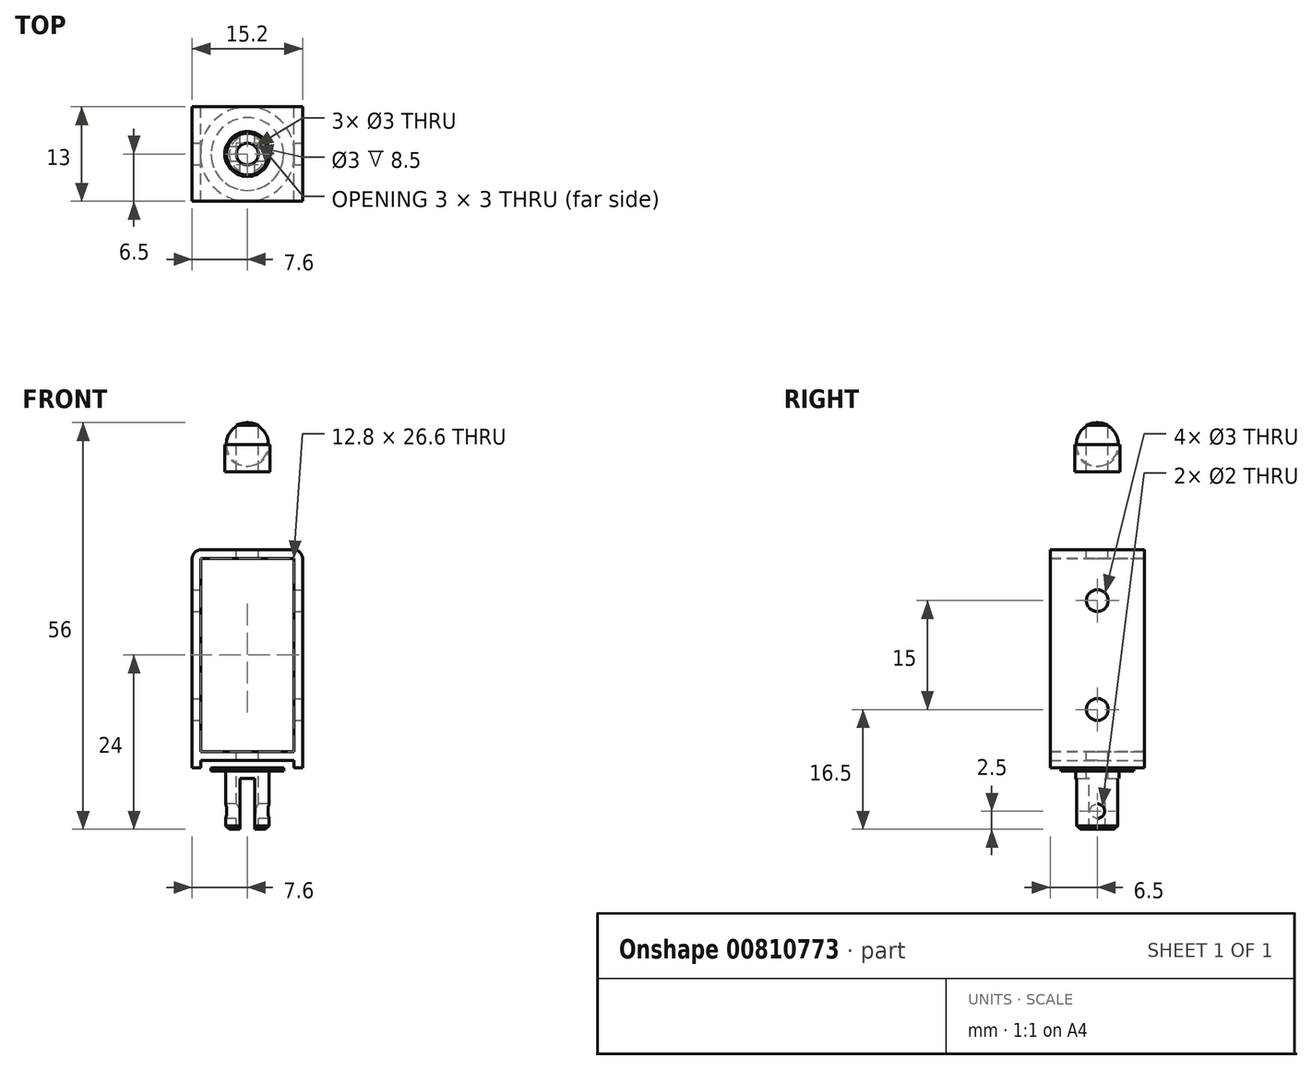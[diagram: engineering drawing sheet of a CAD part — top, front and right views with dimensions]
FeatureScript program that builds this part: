
annotation { "Feature Type Name" : "Feature", "Feature Type Description" : "" }
export const myFeature = defineFeature(function(context is Context, id is Id, definition is map)
    precondition{}
    {
        {
            var Q0;
            Q0=qCreatedBy(makeId("Front.planeOp"),FACE);
            var sketch = newSketch(context, id + "F0", { "sketchPlane" : qUnion([Q0])});
            skLineSegment(sketch, "E0.bottom", {"start": v(7.6, 15) * mm, "end": v(-7.6, 15) * mm});
            skLineSegment(sketch, "E0.top", {"start": v(7.6, -15) * mm, "end": v(-7.6, -15) * mm});
            skLineSegment(sketch, "E0.left", {"start": v(7.6, 15) * mm, "end": v(7.6, -15) * mm});
            skLineSegment(sketch, "E0.right", {"start": v(-7.6, 15) * mm, "end": v(-7.6, -15) * mm});
            skPoint(sketch, "E0.middle", {"position": v(0, 0) * mm});
            skSolve(sketch);
        }
        {
            var Q0;
            Q0=qSketchRegion(id+"F0",true);
            extrude(context, id + "F1", {"entities" : qUnion([Q0]), "depth" : 13 * mm, "symmetric" : true});
        }
        {
            var Q0;
            Q0=qCreatedBy(makeId("Right.planeOp"),FACE);
            var sketch = newSketch(context, id + "F2", { "sketchPlane" : qUnion([Q0])});
            skLineSegment(sketch, "E1", {"start": v(0, 32.5) * mm, "end": v(0, -23.5) * mm});
            skLineSegment(sketch, "E2", {"start": v(0, -23.5) * mm, "end": v(-3, -23.5) * mm});
            skLineSegment(sketch, "E3", {"start": v(-3, -23.5) * mm, "end": v(-3, -15.5) * mm});
            skLineSegment(sketch, "E4", {"start": v(-3, -15.5) * mm, "end": v(-5, -15.5) * mm});
            skLineSegment(sketch, "E5", {"start": v(-5, -15.5) * mm, "end": v(-5, -14.8) * mm});
            skLineSegment(sketch, "E6", {"start": v(-5, -14.8) * mm, "end": v(-1.5, -14.8) * mm});
            skLineSegment(sketch, "E7", {"start": v(-1.5, -14.8) * mm, "end": v(-1.5, 25.75) * mm});
            skLineSegment(sketch, "E8", {"start": v(-1.5, 25.75) * mm, "end": v(-3.1, 25.75) * mm});
            skLineSegment(sketch, "E9", {"start": v(-3.1, 25.75) * mm, "end": v(-3.1, 32.5) * mm});
            skLineSegment(sketch, "E10", {"start": v(-3.1, 32.5) * mm, "end": v(0, 32.5) * mm});
            skSolve(sketch);
        }
        {
            var Q0;
            Q0=qSketchRegion(id+"F2",true);
            var Q1;
            Q1=sQuery(id+"F2.wireOp",EDGE,"E1");
            revolve(context, id + "F3", {"entities" : qUnion([Q0]), "axis" : qUnion([Q1]), "revolveType" : RevolveType.FULL});
        }
        {
            var Q0;
            Q0=makeQuery(id+"F3.opRevolve","SWEPT_EDGE",EDGE,{"disambiguationData":[OSD([sQuery(id+"F2.wireOp",EDGE,"E9"),sQuery(id+"F2.wireOp",EDGE,"E10")])]});
            fillet(context, id + "F4", {"entities" : qUnion([Q0]), "radius" : 3 * mm, "tangentPropagation" : true, "allowEdgeOverflow" : false});
        }
        {
            var Q0;
            Q0=qCreatedBy(makeId("Right.planeOp"),FACE);
            var sketch = newSketch(context, id + "F5", { "sketchPlane" : qUnion([Q0])});
            skLineSegment(sketch, "E11", {"start": v(0, 8) * mm, "end": v(0, -7) * mm, "construction": true});
            skCircle(sketch, "E12", {"center": v(0, 8) * mm, "radius": 1.5 * mm});
            skCircle(sketch, "E13", {"center": v(0, -7) * mm, "radius": 1.5 * mm});
            skLineSegment(sketch, "E14", {"start": v(0, -7) * mm, "end": v(0, -21) * mm, "construction": true});
            skCircle(sketch, "E15", {"center": v(0, -21) * mm, "radius": 1 * mm});
            skSolve(sketch);
        }
        {
            var Q0;
            Q0=makeQuery(id+"F5.imprint","IMPRINT",FACE,{"disambiguationData":[TD([[makeQuery(id+"F5.imprint","IMPRINT",EDGE,{"derivedFrom":sQuery(id+"F5.wireOp",EDGE,"E13")}),1.0]])]});
            var Q1;
            Q1=makeQuery(id+"F5.imprint","IMPRINT",FACE,{"disambiguationData":[TD([[makeQuery(id+"F5.imprint","IMPRINT",EDGE,{"derivedFrom":sQuery(id+"F5.wireOp",EDGE,"E12")}),1.0]])]});
            extrude(context, id + "F6", {"entities" : qUnion([Q0, Q1]), "operationType" : NewBodyOperationType.REMOVE, "endBound" : BoundingType.THROUGH_ALL, "oppositeDirection" : true, "depth" : 25 * mm, "hasSecondDirection" : true, "secondDirectionBound" : BoundingType.THROUGH_ALL, "secondDirectionOppositeDirection" : false, "secondDirectionDepth" : 25 * mm});
        }
        {
            var Q0;
            Q0=makeQuery(id+"F5.imprint","IMPRINT",FACE,{"disambiguationData":[TD([[makeQuery(id+"F5.imprint","IMPRINT",EDGE,{"derivedFrom":sQuery(id+"F5.wireOp",EDGE,"E15")}),1.0]])]});
            extrude(context, id + "F7", {"entities" : qUnion([Q0]), "operationType" : NewBodyOperationType.REMOVE, "endBound" : BoundingType.THROUGH_ALL, "depth" : 25 * mm, "hasSecondDirection" : true, "secondDirectionBound" : BoundingType.THROUGH_ALL, "secondDirectionOppositeDirection" : true, "secondDirectionDepth" : 25 * mm});
        }
        {
            var Q0;
            Q0=qCreatedBy(makeId("Front.planeOp"),FACE);
            var sketch = newSketch(context, id + "F8", { "sketchPlane" : qUnion([Q0])});
            skLineSegment(sketch, "E16.bottom", {"start": v(1, -23.5) * mm, "end": v(-1, -23.5) * mm});
            skLineSegment(sketch, "E16.top", {"start": v(1, -16.5) * mm, "end": v(-1, -16.5) * mm});
            skLineSegment(sketch, "E16.left", {"start": v(1, -23.5) * mm, "end": v(1, -16.5) * mm});
            skLineSegment(sketch, "E16.right", {"start": v(-1, -23.5) * mm, "end": v(-1, -16.5) * mm});
            skPoint(sketch, "E16.middle", {"position": v(0, -20) * mm});
            skSolve(sketch);
        }
        {
            var Q0;
            Q0=makeQuery(id+"F3.opRevolve","SWEPT_EDGE",EDGE,{"disambiguationData":[OSD([sQuery(id+"F2.wireOp",EDGE,"E2"),sQuery(id+"F2.wireOp",EDGE,"E3")])]});
            chamfer(context, id + "F9", {"entities" : qUnion([Q0]), "width" : .5 * mm, "tangentPropagation" : true});
        }
        {
            var Q0;
            Q0=qSketchRegion(id+"F8",true);
            extrude(context, id + "F10", {"entities" : qUnion([Q0]), "operationType" : NewBodyOperationType.REMOVE, "endBound" : BoundingType.THROUGH_ALL, "depth" : 25 * mm, "hasSecondDirection" : true, "secondDirectionBound" : BoundingType.THROUGH_ALL, "secondDirectionOppositeDirection" : true, "secondDirectionDepth" : 25 * mm});
        }
        {
            var Q0;
            Q0=qCreatedBy(makeId("Top.planeOp"),FACE);
            var sketch = newSketch(context, id + "F11", { "sketchPlane" : qUnion([Q0])});
            skCircle(sketch, "E17.0", {"center": v(0, 0) * mm, "radius": 1.5 * mm});
            skSolve(sketch);
        }
        {
            var Q0;
            Q0=qSketchRegion(id+"F11",true);
            extrude(context, id + "F12", {"entities" : qUnion([Q0]), "operationType" : NewBodyOperationType.REMOVE, "endBound" : BoundingType.THROUGH_ALL, "oppositeDirection" : true, "depth" : 25 * mm, "hasSecondDirection" : true, "secondDirectionBound" : BoundingType.THROUGH_ALL, "secondDirectionOppositeDirection" : false, "secondDirectionDepth" : 25 * mm});
        }
        {
            var Q0;
            Q0=makeQuery(id+"F1.opExtrude","SWEPT_EDGE",EDGE,{"disambiguationData":[OSD([sQuery(id+"F0.wireOp",EDGE,"E0.bottom"),sQuery(id+"F0.wireOp",EDGE,"E0.left")])]});
            var Q1;
            Q1=makeQuery(id+"F1.opExtrude","SWEPT_EDGE",EDGE,{"disambiguationData":[OSD([sQuery(id+"F0.wireOp",EDGE,"E0.bottom"),sQuery(id+"F0.wireOp",EDGE,"E0.right")])]});
            fillet(context, id + "F13", {"entities" : qUnion([Q0, Q1]), "radius" : 1.2 * mm, "tangentPropagation" : true, "allowEdgeOverflow" : false});
        }
        {
            var Q0;
            Q0=makeQuery(id+"F1.opExtrude","CAP_FACE",FACE,{"disambiguationData":[OSD([sQuery(id+"F0.wireOp",EDGE,"E0.bottom"),sQuery(id+"F0.wireOp",EDGE,"E0.top"),sQuery(id+"F0.wireOp",EDGE,"E0.left"),sQuery(id+"F0.wireOp",EDGE,"E0.right")])],"isStart":true});
            var sketch = newSketch(context, id + "F14", { "sketchPlane" : qUnion([Q0])});
            skLineSegment(sketch, "E18.bottom", {"start": v(6.4, 13.8) * mm, "end": v(-6.4, 13.8) * mm});
            skLineSegment(sketch, "E18.top", {"start": v(6.4, -12.8) * mm, "end": v(-6.4, -12.8) * mm});
            skLineSegment(sketch, "E18.left", {"start": v(6.4, 13.8) * mm, "end": v(6.4, -12.8) * mm});
            skLineSegment(sketch, "E18.right", {"start": v(-6.4, 13.8) * mm, "end": v(-6.4, -12.8) * mm});
            skPoint(sketch, "E18.middle", {"position": v(0, 0.5) * mm});
            skLineSegment(sketch, "E19.bottom", {"start": v(-6.4, -15) * mm, "end": v(6.4, -15) * mm});
            skLineSegment(sketch, "E19.top", {"start": v(-6.4, -14) * mm, "end": v(6.4, -14) * mm});
            skLineSegment(sketch, "E19.left", {"start": v(-6.4, -15) * mm, "end": v(-6.4, -14) * mm});
            skLineSegment(sketch, "E19.right", {"start": v(6.4, -15) * mm, "end": v(6.4, -14) * mm});
            skLineSegment(sketch, "E20", {"start": v(-6.4, -12.8) * mm, "end": v(-6.4, -14) * mm, "construction": true});
            skLineSegment(sketch, "E21", {"start": v(-6.4, -15) * mm, "end": v(-7.6, -15) * mm, "construction": true});
            skSolve(sketch);
        }
        {
            var Q0;
            Q0=qSketchRegion(id+"F14",true);
            extrude(context, id + "F15", {"entities" : qUnion([Q0]), "operationType" : NewBodyOperationType.REMOVE, "endBound" : BoundingType.THROUGH_ALL, "oppositeDirection" : true, "depth" : 25 * mm, "hasSecondDirection" : true, "secondDirectionBound" : BoundingType.THROUGH_ALL, "secondDirectionOppositeDirection" : false, "secondDirectionDepth" : 25 * mm});
        }
        {
            var Q0;
            Q0=qCreatedBy(makeId("Top.planeOp"),FACE);
            var sketch = newSketch(context, id + "F16", { "sketchPlane" : qUnion([Q0])});
            skCircle(sketch, "E22", {"center": v(0, 0) * mm, "radius": 6.5 * mm});
            skSolve(sketch);
        }
        {
            var Q0;
            Q0=qSketchRegion(id+"F16",true);
            var Q1;
            Q1=makeQuery(id+"F15.boolean.opBoolean","COPY",FACE,{"derivedFrom":makeQuery(id+"F15.opExtrude","SWEPT_FACE",FACE,{"disambiguationData":[OSD([sQuery(id+"F14.wireOp",EDGE,"E18.bottom")])]})});
            var Q2;
            Q2=makeQuery(id+"F15.boolean.opBoolean","COPY",FACE,{"derivedFrom":makeQuery(id+"F15.opExtrude","SWEPT_FACE",FACE,{"disambiguationData":[OSD([sQuery(id+"F14.wireOp",EDGE,"E18.top")])]})});
            extrude(context, id + "F17", {"entities" : qUnion([Q0]), "endBound" : BoundingType.UP_TO_SURFACE, "endBoundEntityFace" : qUnion([Q1]), "depth" : 25 * mm, "hasSecondDirection" : true, "secondDirectionBound" : BoundingType.UP_TO_SURFACE, "secondDirectionOppositeDirection" : true, "secondDirectionBoundEntityFace" : qUnion([Q2]), "secondDirectionDepth" : 25 * mm});
        }
    });
